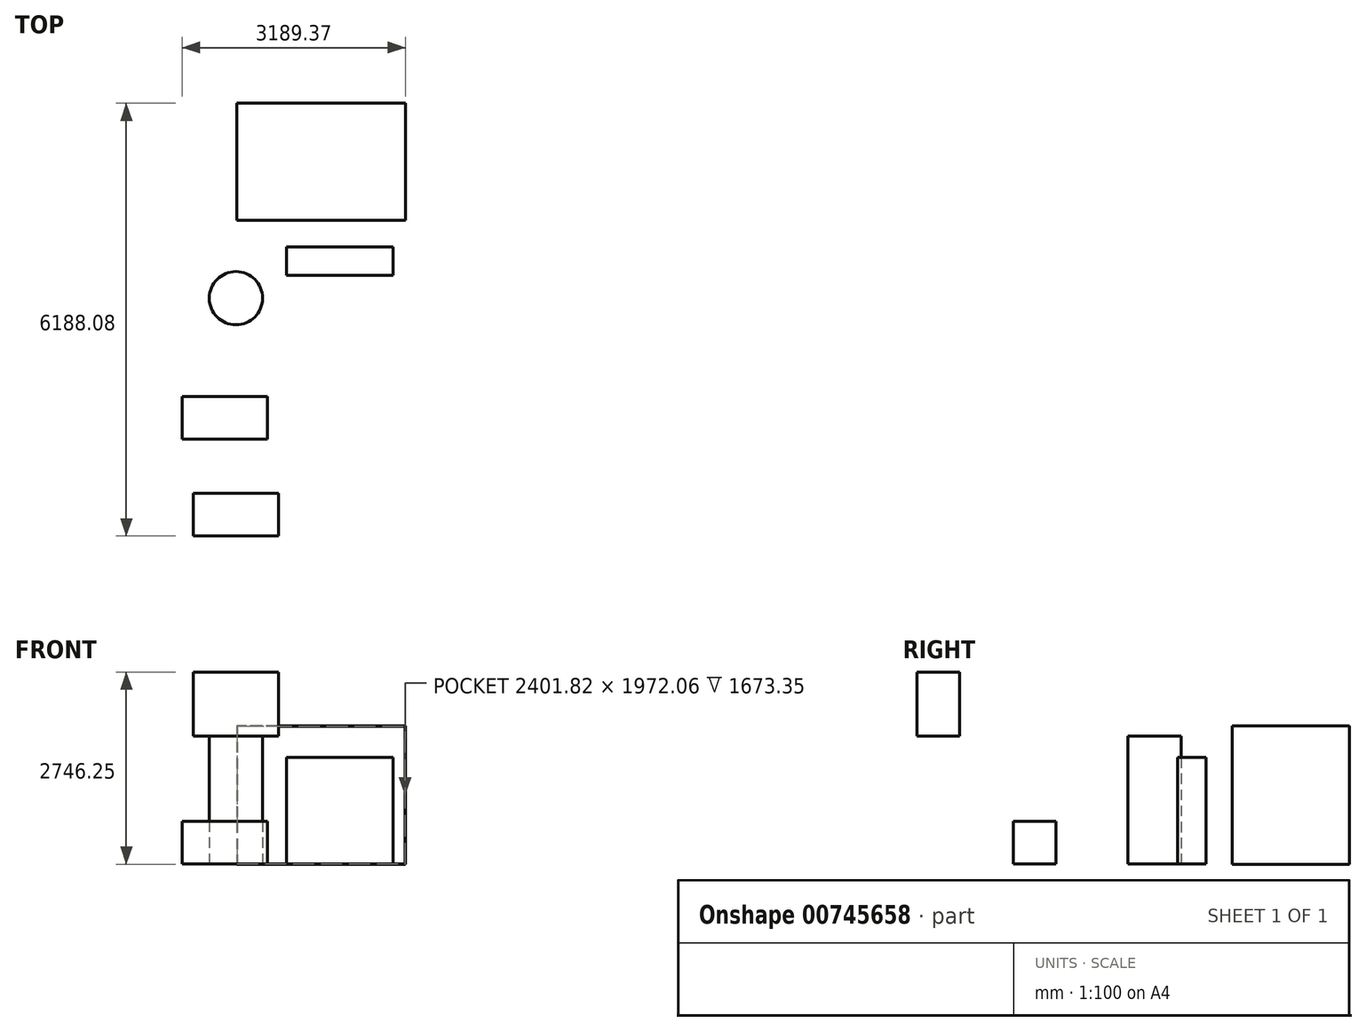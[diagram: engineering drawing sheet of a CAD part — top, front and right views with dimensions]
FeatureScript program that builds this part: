
annotation { "Feature Type Name" : "Feature", "Feature Type Description" : "" }
export const myFeature = defineFeature(function(context is Context, id is Id, definition is map)
    precondition{}
    {
        {
            var Q0;
            Q0=qCreatedBy(makeId("Top.planeOp"),FACE);
            var sketch = newSketch(context, id + "F0", { "sketchPlane" : qUnion([Q0])});
            skLineSegment(sketch, "E0.bottom", {"start": v(1203.96, -838.2) * mm, "end": v(-1203.96, -838.2) * mm});
            skLineSegment(sketch, "E0.top", {"start": v(1203.96, 838.2) * mm, "end": v(-1203.96, 838.2) * mm});
            skLineSegment(sketch, "E0.left", {"start": v(1203.96, -838.2) * mm, "end": v(1203.96, 838.2) * mm});
            skLineSegment(sketch, "E0.right", {"start": v(-1203.96, -838.2) * mm, "end": v(-1203.96, 838.2) * mm});
            skPoint(sketch, "E0.middle", {"position": v(0, 0) * mm});
            skSolve(sketch);
        }
        {
            var Q0;
            Q0=makeQuery(id+"F0.imprint","IMPRINT",FACE,{"disambiguationData":[TD([[makeQuery(id+"F0.imprint","IMPRINT",EDGE,{"derivedFrom":sQuery(id+"F0.wireOp",EDGE,"E0.bottom")}),-1.0]])]});
            extrude(context, id + "F1", {"entities" : qUnion([Q0]), "depth" : 1978.15 * mm, "offsetDistance" : 30.48 * mm});
        }
        {
            var Q0;
            Q0=makeQuery(id+"F1.opExtrude","SWEPT_FACE",FACE,{"disambiguationData":[OSD([sQuery(id+"F0.wireOp",EDGE,"E0.bottom")])]});
            shell(context, id + "F2", {"entities" : qUnion([Q0]), "thickness" : 3.05 * mm});
        }
        {
            var Q0;
            {var subQ0=sQuery(id+"F0.wireOp",EDGE,"E0.right");var subQ1=sQuery(id+"F0.wireOp",EDGE,"E0.left");var subQ2=sQuery(id+"F0.wireOp",EDGE,"E0.top");var subQ3=sQuery(id+"F0.wireOp",EDGE,"E0.bottom");Q0=makeQuery(id+"F2.opShell","OFFSET_FACE",FACE,{"disambiguationData":[OSD([subQ3,subQ2,subQ1,subQ0]),TDD([makeQuery(id+"F1.opExtrude","CAP_FACE",FACE,{"disambiguationData":[OSD([subQ3,subQ2,subQ1,subQ0])],"isStart":true})])]});}
            var sketch = newSketch(context, id + "F3", { "sketchPlane" : qUnion([Q0])});
            skCircle(sketch, "E1", {"center": v(-1217.76, -1948.87) * mm, "radius": 381 * mm});
            skSolve(sketch);
        }
        {
            var Q0;
            Q0=makeQuery(id+"F3.imprint","IMPRINT",FACE,{"disambiguationData":[TD([[makeQuery(id+"F3.imprint","IMPRINT",EDGE,{"derivedFrom":sQuery(id+"F3.wireOp",EDGE,"E1")}),1.0]])]});
            extrude(context, id + "F4", {"entities" : qUnion([Q0]), "depth" : 1828.8 * mm, "offsetDistance" : 30.48 * mm});
        }
        {
            var Q0;
            {var subQ0=sQuery(id+"F0.wireOp",EDGE,"E0.right");var subQ1=sQuery(id+"F0.wireOp",EDGE,"E0.left");var subQ2=sQuery(id+"F0.wireOp",EDGE,"E0.top");var subQ3=sQuery(id+"F0.wireOp",EDGE,"E0.bottom");Q0=makeQuery(id+"F2.opShell","OFFSET_FACE",FACE,{"disambiguationData":[OSD([subQ3,subQ2,subQ1,subQ0]),TDD([makeQuery(id+"F1.opExtrude","CAP_FACE",FACE,{"disambiguationData":[OSD([subQ3,subQ2,subQ1,subQ0])],"isStart":true})])]});}
            var sketch = newSketch(context, id + "F5", { "sketchPlane" : qUnion([Q0])});
            skLineSegment(sketch, "E2.bottom", {"start": v(1029.4, -1621.25) * mm, "end": v(-494.6, -1621.25) * mm});
            skLineSegment(sketch, "E2.top", {"start": v(1029.4, -1214.85) * mm, "end": v(-494.6, -1214.85) * mm});
            skLineSegment(sketch, "E2.left", {"start": v(1029.4, -1621.25) * mm, "end": v(1029.4, -1214.85) * mm});
            skLineSegment(sketch, "E2.right", {"start": v(-494.6, -1621.25) * mm, "end": v(-494.6, -1214.85) * mm});
            skPoint(sketch, "E2.middle", {"position": v(267.4, -1418.05) * mm});
            skSolve(sketch);
        }
        {
            var Q0;
            Q0=makeQuery(id+"F5.imprint","IMPRINT",FACE,{"disambiguationData":[TD([[makeQuery(id+"F5.imprint","IMPRINT",EDGE,{"derivedFrom":sQuery(id+"F5.wireOp",EDGE,"E2.bottom")}),-1.0]])]});
            extrude(context, id + "F6", {"entities" : qUnion([Q0]), "depth" : 1524 * mm, "offsetDistance" : 30.48 * mm});
        }
        {
            var Q0;
            Q0=makeQuery(id+"F4.opExtrude","CAP_FACE",FACE,{"disambiguationData":[OSD([sQuery(id+"F3.wireOp",EDGE,"E1")])],"isStart":false});
            var sketch = newSketch(context, id + "F7", { "sketchPlane" : qUnion([Q0])});
            skLineSegment(sketch, "E3.bottom", {"start": v(-608.41, -5349.88) * mm, "end": v(-1827.61, -5349.88) * mm});
            skLineSegment(sketch, "E3.top", {"start": v(-608.41, -4740.28) * mm, "end": v(-1827.61, -4740.28) * mm});
            skLineSegment(sketch, "E3.left", {"start": v(-608.41, -5349.88) * mm, "end": v(-608.41, -4740.28) * mm});
            skLineSegment(sketch, "E3.right", {"start": v(-1827.61, -5349.88) * mm, "end": v(-1827.61, -4740.28) * mm});
            skPoint(sketch, "E3.middle", {"position": v(-1218.01, -5045.08) * mm});
            skSolve(sketch);
        }
        {
            var Q0;
            Q0=makeQuery(id+"F7.imprint","IMPRINT",FACE,{"disambiguationData":[TD([[makeQuery(id+"F7.imprint","IMPRINT",EDGE,{"derivedFrom":sQuery(id+"F7.wireOp",EDGE,"E3.bottom")}),-1.0]])]});
            extrude(context, id + "F8", {"entities" : qUnion([Q0]), "depth" : 914.4 * mm, "offsetDistance" : 30.48 * mm});
        }
        {
            var Q0;
            {var subQ0=sQuery(id+"F0.wireOp",EDGE,"E0.right");var subQ1=sQuery(id+"F0.wireOp",EDGE,"E0.left");var subQ2=sQuery(id+"F0.wireOp",EDGE,"E0.top");var subQ3=sQuery(id+"F0.wireOp",EDGE,"E0.bottom");Q0=makeQuery(id+"F2.opShell","OFFSET_FACE",FACE,{"disambiguationData":[OSD([subQ3,subQ2,subQ1,subQ0]),TDD([makeQuery(id+"F1.opExtrude","CAP_FACE",FACE,{"disambiguationData":[OSD([subQ3,subQ2,subQ1,subQ0])],"isStart":true})])]});}
            var sketch = newSketch(context, id + "F9", { "sketchPlane" : qUnion([Q0])});
            skLineSegment(sketch, "E4.bottom", {"start": v(-766.2, -3357.06) * mm, "end": v(-1985.4, -3357.06) * mm});
            skLineSegment(sketch, "E4.top", {"start": v(-766.2, -3966.66) * mm, "end": v(-1985.4, -3966.66) * mm});
            skLineSegment(sketch, "E4.left", {"start": v(-766.2, -3357.06) * mm, "end": v(-766.2, -3966.66) * mm});
            skLineSegment(sketch, "E4.right", {"start": v(-1985.4, -3357.06) * mm, "end": v(-1985.4, -3966.66) * mm});
            skPoint(sketch, "E4.middle", {"position": v(-1375.8, -3661.86) * mm});
            skSolve(sketch);
        }
        {
            var Q0;
            Q0=makeQuery(id+"F9.imprint","IMPRINT",FACE,{"disambiguationData":[TD([[makeQuery(id+"F9.imprint","IMPRINT",EDGE,{"derivedFrom":sQuery(id+"F9.wireOp",EDGE,"E4.bottom")}),1.0]])]});
            extrude(context, id + "F10", {"entities" : qUnion([Q0]), "depth" : 609.6 * mm, "offsetDistance" : 30.48 * mm});
        }
    });
